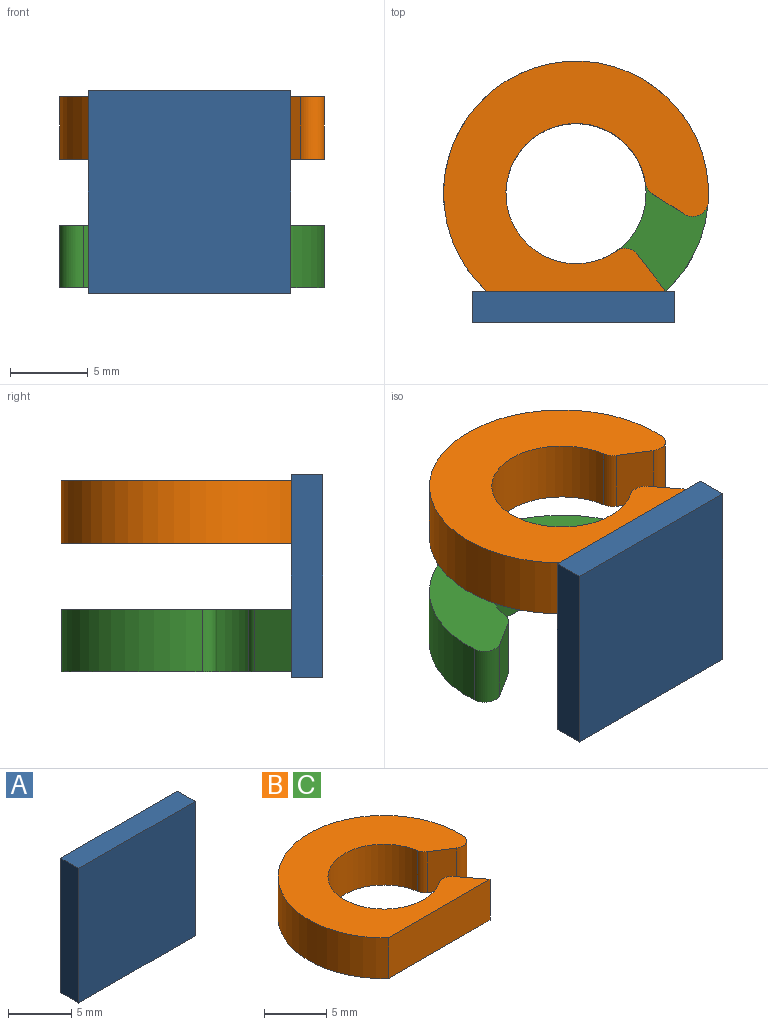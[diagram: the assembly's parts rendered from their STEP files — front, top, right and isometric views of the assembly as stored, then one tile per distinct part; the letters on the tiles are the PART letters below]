
ASSEMBLY  parts=3 mates=2
PART A: 6 faces, bbox 13x2x13 mm
  f0: plane 13x2mm, normal (0,0,-1), area 26mm2, adj f1,f3,f4,f5
  f1: plane 13x2mm, normal (1,0,0), area 26mm2, adj f0,f2,f4,f5
  f2: plane 13x2mm, normal (0,0,1), area 26mm2, adj f1,f3,f4,f5
  f3: plane 13x2mm, normal (-1,0,0), area 26mm2, adj f0,f2,f4,f5
  f4: plane 13x13mm, normal (0,-1,0), area 169mm2, adj f0,f1,f2,f3
  f5: plane 13x13mm, normal (0,1,0), area 169mm2, adj f0,f1,f2,f3
PART B: 10 faces, bbox 17x14.8x4 mm
  f0: cylinder r=8.5mm len=17mm, axis (0,0,1), area 137.1mm2, adj f1,f7,f8,f9
  f1: plane 11.49x4mm, normal (0,-1,0), area 46mm2, adj f0,f2,f8,f9
  f2: plane 4x2.36mm, normal (0.79,0.61,0), area 11.9mm2, adj f1,f3,f8,f9
  f3: cylinder r=1mm len=4mm, axis (0,0,1), area 6.1mm2, adj f2,f4,f8,f9
  f4: cylinder r=4.5mm len=9mm, axis (0,0,1), area 93.1mm2, adj f3,f5,f8,f9
  f5: cylinder r=1mm len=4mm, axis (0,0,1), area 3.4mm2, adj f4,f6,f8,f9
  f6: plane 4x2.05mm, normal (-0.53,-0.85,0), area 9.7mm2, adj f5,f7,f8,f9
  f7: cylinder r=1mm len=4mm, axis (0,0,1), area 8.3mm2, adj f0,f6,f8,f9
  f8: plane 17x14.77mm, normal (0,0,1), area 128mm2, adj f0,f1,f2,f3,f4,f5,f6,f7
  f9: plane 17x14.77mm, normal (0,0,-1), area 128mm2, adj f0,f1,f2,f3,f4,f5,f6,f7
PART C: same geometry as B
PLACE A t=(-7,-8.8,3.78)mm
PLACE B t=(46.37,-14.55,-2.49)mm
PLACE C rot(axis=(0,-1,0),180deg) t=(-36.81,-14.55,-6.76)mm
MATE planar C.f1 <-> A.f5  axis (0,-1,0) through (4.78,-8.8,-8.76)mm
MATE planar B.f1 <-> A.f5  axis (0,-1,0) through (4.79,-8.8,-0.49)mm
